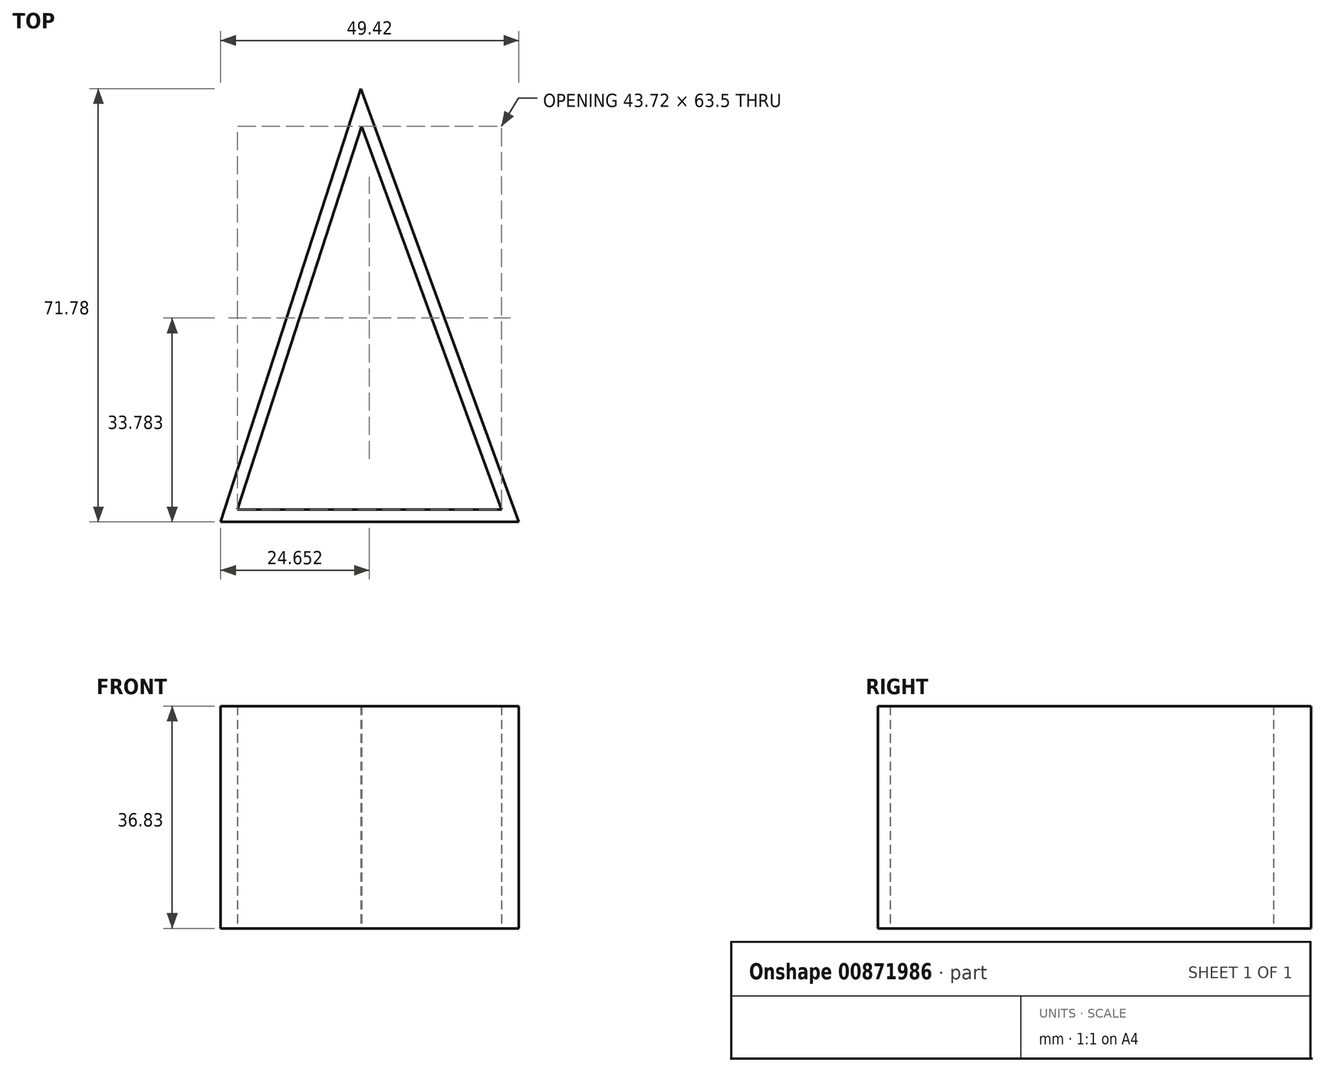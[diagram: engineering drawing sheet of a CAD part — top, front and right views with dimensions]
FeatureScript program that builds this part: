
annotation { "Feature Type Name" : "Feature", "Feature Type Description" : "" }
export const myFeature = defineFeature(function(context is Context, id is Id, definition is map)
    precondition{}
    {
        {
            var Q0;
            Q0=qCreatedBy(makeId("Top.planeOp"),FACE);
            var sketch = newSketch(context, id + "F0", { "sketchPlane" : qUnion([Q0])});
            skLineSegment(sketch, "E0", {"start": v(0, 36.76) * mm, "end": v(0, -26.74) * mm});
            skLineSegment(sketch, "E1", {"start": v(0, 36.76) * mm, "end": v(-20.55, -26.74) * mm});
            skLineSegment(sketch, "E2", {"start": v(-20.55, -26.74) * mm, "end": v(23.17, -26.74) * mm});
            skLineSegment(sketch, "E3", {"start": v(23.17, -26.74) * mm, "end": v(0, 36.76) * mm});
            skLineSegment(sketch, "E4.0", {"start": v(-0.12, 43) * mm, "end": v(-23.34, -28.77) * mm});
            skLineSegment(sketch, "E4.1", {"start": v(26.08, -28.77) * mm, "end": v(-0.12, 43) * mm});
            skLineSegment(sketch, "E4.2", {"start": v(-23.34, -28.77) * mm, "end": v(26.08, -28.77) * mm});
            skSolve(sketch);
        }
        {
            var Q0;
            {var subQ3=sQuery(id+"F0.wireOp",EDGE,"E1");Q0=makeQuery(id+"F0.imprint","IMPRINT",FACE,{"disambiguationData":[TD([[makeQuery(id+"F0.imprint","IMPRINT",EDGE,{"derivedFrom":subQ3}),-1.0]])]});}
            extrude(context, id + "F1", {"entities" : qUnion([Q0]), "depth" : 36.83 * mm, "offsetDistance" : 25.4 * mm});
        }
    });
